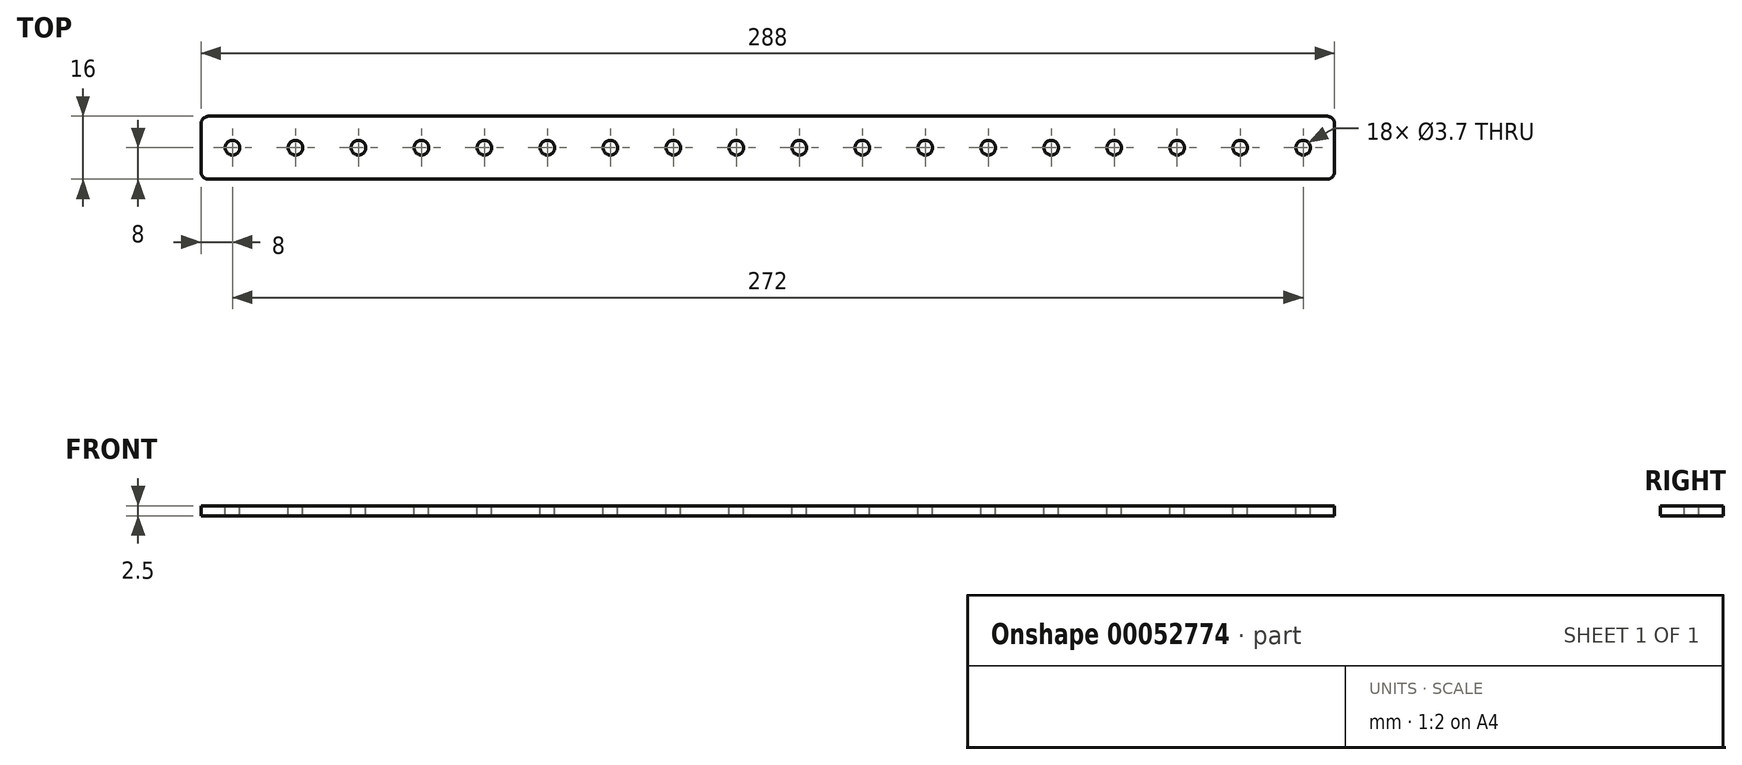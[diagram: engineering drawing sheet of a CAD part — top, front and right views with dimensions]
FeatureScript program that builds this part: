
annotation { "Feature Type Name" : "Feature", "Feature Type Description" : "" }
export const myFeature = defineFeature(function(context is Context, id is Id, definition is map)
    precondition{}
    {
        {
            var Q0;
            Q0=qCreatedBy(makeId("Top.planeOp"),FACE);
            var sketch = newSketch(context, id + "F0", { "sketchPlane" : qUnion([Q0])});
            skLineSegment(sketch, "E0.rect.bottom", {"start": v(142, 8) * mm, "end": v(-142, 8) * mm});
            skLineSegment(sketch, "E0.rect.top", {"start": v(142, -8) * mm, "end": v(-142, -8) * mm});
            skLineSegment(sketch, "E0.rect.left", {"start": v(144, 6) * mm, "end": v(144, -6) * mm});
            skLineSegment(sketch, "E0.rect.right", {"start": v(-144, 6) * mm, "end": v(-144, -6) * mm});
            skPoint(sketch, "E0.rect.middle", {"position": v(0, 0) * mm});
            skPoint(sketch, "E1.visualSharp", {"position": v(-144, 8) * mm});
            skArc(sketch, "E1.filletArc", {"start": v(-142, 8) * mm, "mid": v(-143.41, 7.41) * mm, "end": v(-144, 6) * mm});
            skPoint(sketch, "E2.visualSharp", {"position": v(-144, -8) * mm});
            skArc(sketch, "E2.filletArc", {"start": v(-144, -6) * mm, "mid": v(-143.41, -7.41) * mm, "end": v(-142, -8) * mm});
            skPoint(sketch, "E3.visualSharp", {"position": v(144, 8) * mm});
            skArc(sketch, "E3.filletArc", {"start": v(144, 6) * mm, "mid": v(143.41, 7.41) * mm, "end": v(142, 8) * mm});
            skPoint(sketch, "E4.visualSharp", {"position": v(144, -8) * mm});
            skArc(sketch, "E4.filletArc", {"start": v(142, -8) * mm, "mid": v(143.41, -7.41) * mm, "end": v(144, -6) * mm});
            skSolve(sketch);
        }
        {
            var Q0;
            Q0 = qSketchRegion(id + "F0", true);
            extrude(context, id + "F1", {"entities" : qUnion([Q0]), "depth" : 2.5 * mm});
        }
        {
            var Q0;
            Q0=makeQuery(id+"F1.opExtrude","CAP_FACE",FACE,{"disambiguationData":[OSD([sQuery(id+"F0.wireOp",EDGE,"E0.rect.bottom"),sQuery(id+"F0.wireOp",EDGE,"E0.rect.top"),sQuery(id+"F0.wireOp",EDGE,"E0.rect.left"),sQuery(id+"F0.wireOp",EDGE,"E0.rect.right"),sQuery(id+"F0.wireOp",EDGE,"E1.filletArc"),sQuery(id+"F0.wireOp",EDGE,"E2.filletArc"),sQuery(id+"F0.wireOp",EDGE,"E3.filletArc"),sQuery(id+"F0.wireOp",EDGE,"E4.filletArc")])],"isStart":false});
            var sketch = newSketch(context, id + "F2", { "sketchPlane" : qUnion([Q0])});
            skCircle(sketch, "E5", {"center": v(-136, 0) * mm, "radius": 1.85 * mm});
            skCircle(sketch, "E6.1.0.0", {"center": v(-120, 0) * mm, "radius": 1.85 * mm});
            skCircle(sketch, "E6.2.0.0", {"center": v(-104, 0) * mm, "radius": 1.85 * mm});
            skCircle(sketch, "E6.3.0.0", {"center": v(-88, 0) * mm, "radius": 1.85 * mm});
            skCircle(sketch, "E6.4.0.0", {"center": v(-72, 0) * mm, "radius": 1.85 * mm});
            skCircle(sketch, "E6.5.0.0", {"center": v(-56, 0) * mm, "radius": 1.85 * mm});
            skCircle(sketch, "E6.6.0.0", {"center": v(-40, 0) * mm, "radius": 1.85 * mm});
            skCircle(sketch, "E6.7.0.0", {"center": v(-24, 0) * mm, "radius": 1.85 * mm});
            skCircle(sketch, "E6.8.0.0", {"center": v(-8, 0) * mm, "radius": 1.85 * mm});
            skCircle(sketch, "E6.9.0.0", {"center": v(8, 0) * mm, "radius": 1.85 * mm});
            skCircle(sketch, "E6.10.0.0", {"center": v(24, 0) * mm, "radius": 1.85 * mm});
            skCircle(sketch, "E6.11.0.0", {"center": v(40, 0) * mm, "radius": 1.85 * mm});
            skCircle(sketch, "E6.12.0.0", {"center": v(56, 0) * mm, "radius": 1.85 * mm});
            skCircle(sketch, "E6.13.0.0", {"center": v(72, 0) * mm, "radius": 1.85 * mm});
            skCircle(sketch, "E6.14.0.0", {"center": v(88, 0) * mm, "radius": 1.85 * mm});
            skCircle(sketch, "E6.15.0.0", {"center": v(104, 0) * mm, "radius": 1.85 * mm});
            skCircle(sketch, "E6.16.0.0", {"center": v(120, 0) * mm, "radius": 1.85 * mm});
            skCircle(sketch, "E6.17.0.0", {"center": v(136, 0) * mm, "radius": 1.85 * mm});
            skLineSegment(sketch, "E6.direction1", {"start": v(-136, 0) * mm, "end": v(-120, 0) * mm, "construction": true});
            skSolve(sketch);
        }
        {
            var Q0;
            Q0=sQuery(id+"F2.wireOp",VERTEX,"E5.center");
            var Q1;
            Q1=sQuery(id+"F2.wireOp",VERTEX,"E6.1.0.0.center");
            var Q2;
            Q2=sQuery(id+"F2.wireOp",VERTEX,"E6.2.0.0.center");
            var Q3;
            Q3=sQuery(id+"F2.wireOp",VERTEX,"E6.3.0.0.center");
            var Q4;
            Q4=sQuery(id+"F2.wireOp",VERTEX,"E6.4.0.0.center");
            var Q5;
            Q5=sQuery(id+"F2.wireOp",VERTEX,"E6.5.0.0.center");
            var Q6;
            Q6=sQuery(id+"F2.wireOp",VERTEX,"E6.6.0.0.center");
            var Q7;
            Q7=sQuery(id+"F2.wireOp",VERTEX,"E6.7.0.0.center");
            var Q8;
            Q8=sQuery(id+"F2.wireOp",VERTEX,"E6.8.0.0.center");
            var Q9;
            Q9=sQuery(id+"F2.wireOp",VERTEX,"E6.9.0.0.center");
            var Q10;
            Q10=sQuery(id+"F2.wireOp",VERTEX,"E6.10.0.0.center");
            var Q11;
            Q11=sQuery(id+"F2.wireOp",VERTEX,"E6.11.0.0.center");
            var Q12;
            Q12=sQuery(id+"F2.wireOp",VERTEX,"E6.12.0.0.center");
            var Q13;
            Q13=sQuery(id+"F2.wireOp",VERTEX,"E6.13.0.0.center");
            var Q14;
            Q14=sQuery(id+"F2.wireOp",VERTEX,"E6.14.0.0.center");
            var Q15;
            Q15=sQuery(id+"F2.wireOp",VERTEX,"E6.14.0.0.center");
            var Q16;
            Q16=sQuery(id+"F2.wireOp",VERTEX,"E6.15.0.0.center");
            var Q17;
            Q17=sQuery(id+"F2.wireOp",VERTEX,"E6.16.0.0.center");
            var Q18;
            Q18=sQuery(id+"F2.wireOp",VERTEX,"E6.17.0.0.center");
            var Q19;
            Q19=makeQuery(id+"F1.opExtrude","SWEPT_BODY",BODY,{"disambiguationData":[OSD([sQuery(id+"F0.wireOp",EDGE,"E0.rect.bottom"),sQuery(id+"F0.wireOp",EDGE,"E0.rect.top"),sQuery(id+"F0.wireOp",EDGE,"E0.rect.left"),sQuery(id+"F0.wireOp",EDGE,"E0.rect.right"),sQuery(id+"F0.wireOp",EDGE,"E1.filletArc"),sQuery(id+"F0.wireOp",EDGE,"E2.filletArc"),sQuery(id+"F0.wireOp",EDGE,"E3.filletArc"),sQuery(id+"F0.wireOp",EDGE,"E4.filletArc")])]});
            hole(context, id + "F3", {"style" : HoleStyle.SIMPLE, "holeDiameter" : 3.7 * mm, "endStyle" : HoleEndStyle.THROUGH, "locations" : qUnion([Q0, Q1, Q2, Q3, Q4, Q5, Q6, Q7, Q8, Q9, Q10, Q11, Q12, Q13, Q14, Q15, Q16, Q17, Q18]), "scope" : qUnion([Q19])});
        }
    });
